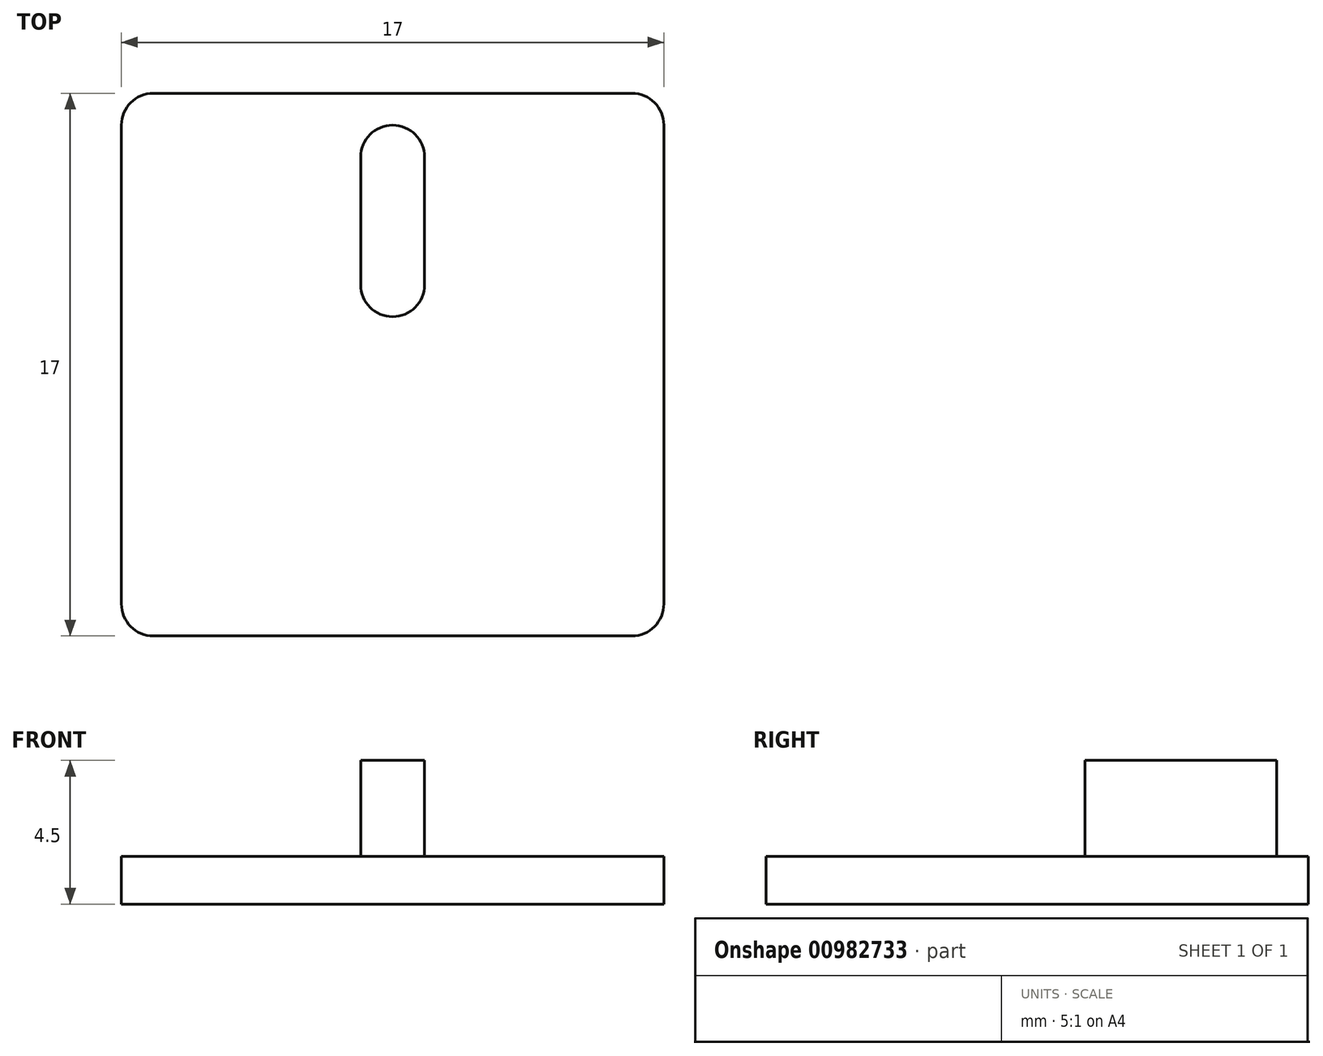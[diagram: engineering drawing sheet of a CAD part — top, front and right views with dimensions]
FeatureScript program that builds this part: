
annotation { "Feature Type Name" : "Feature", "Feature Type Description" : "" }
export const myFeature = defineFeature(function(context is Context, id is Id, definition is map)
    precondition{}
    {
        {
            var Q0;
            Q0=qCreatedBy(makeId("Top.planeOp"),FACE);
            var sketch = newSketch(context, id + "F0", { "sketchPlane" : qUnion([Q0])});
            skLineSegment(sketch, "E0.bottom", {"start": v(8.5, 8.5) * mm, "end": v(-8.5, 8.5) * mm});
            skLineSegment(sketch, "E0.top", {"start": v(8.5, -8.5) * mm, "end": v(-8.5, -8.5) * mm});
            skLineSegment(sketch, "E0.left", {"start": v(8.5, 8.5) * mm, "end": v(8.5, -8.5) * mm});
            skLineSegment(sketch, "E0.right", {"start": v(-8.5, 8.5) * mm, "end": v(-8.5, -8.5) * mm});
            skPoint(sketch, "E0.middle", {"position": v(0, 0) * mm});
            skSolve(sketch);
        }
        {
            var Q0;
            Q0=makeQuery(id+"F0.imprint","IMPRINT",FACE,{"disambiguationData":[TD([[makeQuery(id+"F0.imprint","IMPRINT",EDGE,{"derivedFrom":sQuery(id+"F0.wireOp",EDGE,"E0.bottom")}),1.0]])]});
            extrude(context, id + "F1", {"entities" : qUnion([Q0]), "depth" : 1.5 * mm, "offsetDistance" : 25 * mm});
        }
        {
            var Q0;
            Q0=makeQuery(id+"F1.opExtrude","CAP_FACE",FACE,{"disambiguationData":[OSD([sQuery(id+"F0.wireOp",EDGE,"E0.bottom"),sQuery(id+"F0.wireOp",EDGE,"E0.top"),sQuery(id+"F0.wireOp",EDGE,"E0.left"),sQuery(id+"F0.wireOp",EDGE,"E0.right")])],"isStart":false});
            var sketch = newSketch(context, id + "F2", { "sketchPlane" : qUnion([Q0])});
            skLineSegment(sketch, "E1.bottom", {"start": v(1, 6.5) * mm, "end": v(-1, 6.5) * mm});
            skLineSegment(sketch, "E1.top", {"start": v(1, 2.5) * mm, "end": v(-1, 2.5) * mm});
            skLineSegment(sketch, "E1.left", {"start": v(1, 6.5) * mm, "end": v(1, 2.5) * mm});
            skLineSegment(sketch, "E1.right", {"start": v(-1, 6.5) * mm, "end": v(-1, 2.5) * mm});
            skArc(sketch, "E2", {"start": v(-1, 6.5) * mm, "mid": v(0, 7.5) * mm, "end": v(1, 6.5) * mm});
            skArc(sketch, "E3", {"start": v(-1, 2.5) * mm, "mid": v(0, 1.5) * mm, "end": v(1, 2.5) * mm});
            skSolve(sketch);
        }
        {
            var Q0;
            Q0=makeQuery(id+"F2.imprint","IMPRINT",FACE,{"disambiguationData":[TD([[makeQuery(id+"F2.imprint","IMPRINT",EDGE,{"derivedFrom":sQuery(id+"F2.wireOp",EDGE,"E1.top")}),1.0]])]});
            var Q1;
            Q1=makeQuery(id+"F2.imprint","IMPRINT",FACE,{"disambiguationData":[TD([[makeQuery(id+"F2.imprint","IMPRINT",EDGE,{"derivedFrom":sQuery(id+"F2.wireOp",EDGE,"E1.bottom")}),1.0]])]});
            var Q2;
            Q2=makeQuery(id+"F2.imprint","IMPRINT",FACE,{"disambiguationData":[TD([[makeQuery(id+"F2.imprint","IMPRINT",EDGE,{"derivedFrom":sQuery(id+"F2.wireOp",EDGE,"E1.bottom")}),-1.0]])]});
            extrude(context, id + "F3", {"entities" : qUnion([Q0, Q1, Q2]), "operationType" : NewBodyOperationType.ADD, "depth" : 3 * mm, "offsetDistance" : 25 * mm});
        }
        {
            var Q0;
            Q0=makeQuery(id+"F1.opExtrude","SWEPT_EDGE",EDGE,{"disambiguationData":[OSD([sQuery(id+"F0.wireOp",EDGE,"E0.bottom"),sQuery(id+"F0.wireOp",EDGE,"E0.right")])]});
            var Q1;
            Q1=makeQuery(id+"F1.opExtrude","SWEPT_EDGE",EDGE,{"disambiguationData":[OSD([sQuery(id+"F0.wireOp",EDGE,"E0.top"),sQuery(id+"F0.wireOp",EDGE,"E0.right")])]});
            var Q2;
            Q2=makeQuery(id+"F1.opExtrude","SWEPT_EDGE",EDGE,{"disambiguationData":[OSD([sQuery(id+"F0.wireOp",EDGE,"E0.bottom"),sQuery(id+"F0.wireOp",EDGE,"E0.left")])]});
            var Q3;
            Q3=makeQuery(id+"F1.opExtrude","SWEPT_EDGE",EDGE,{"disambiguationData":[OSD([sQuery(id+"F0.wireOp",EDGE,"E0.top"),sQuery(id+"F0.wireOp",EDGE,"E0.left")])]});
            fillet(context, id + "F4", {"entities" : qUnion([Q0, Q1, Q2, Q3]), "radius" : 1 * mm, "tangentPropagation" : true, "allowEdgeOverflow" : false});
        }
    });
